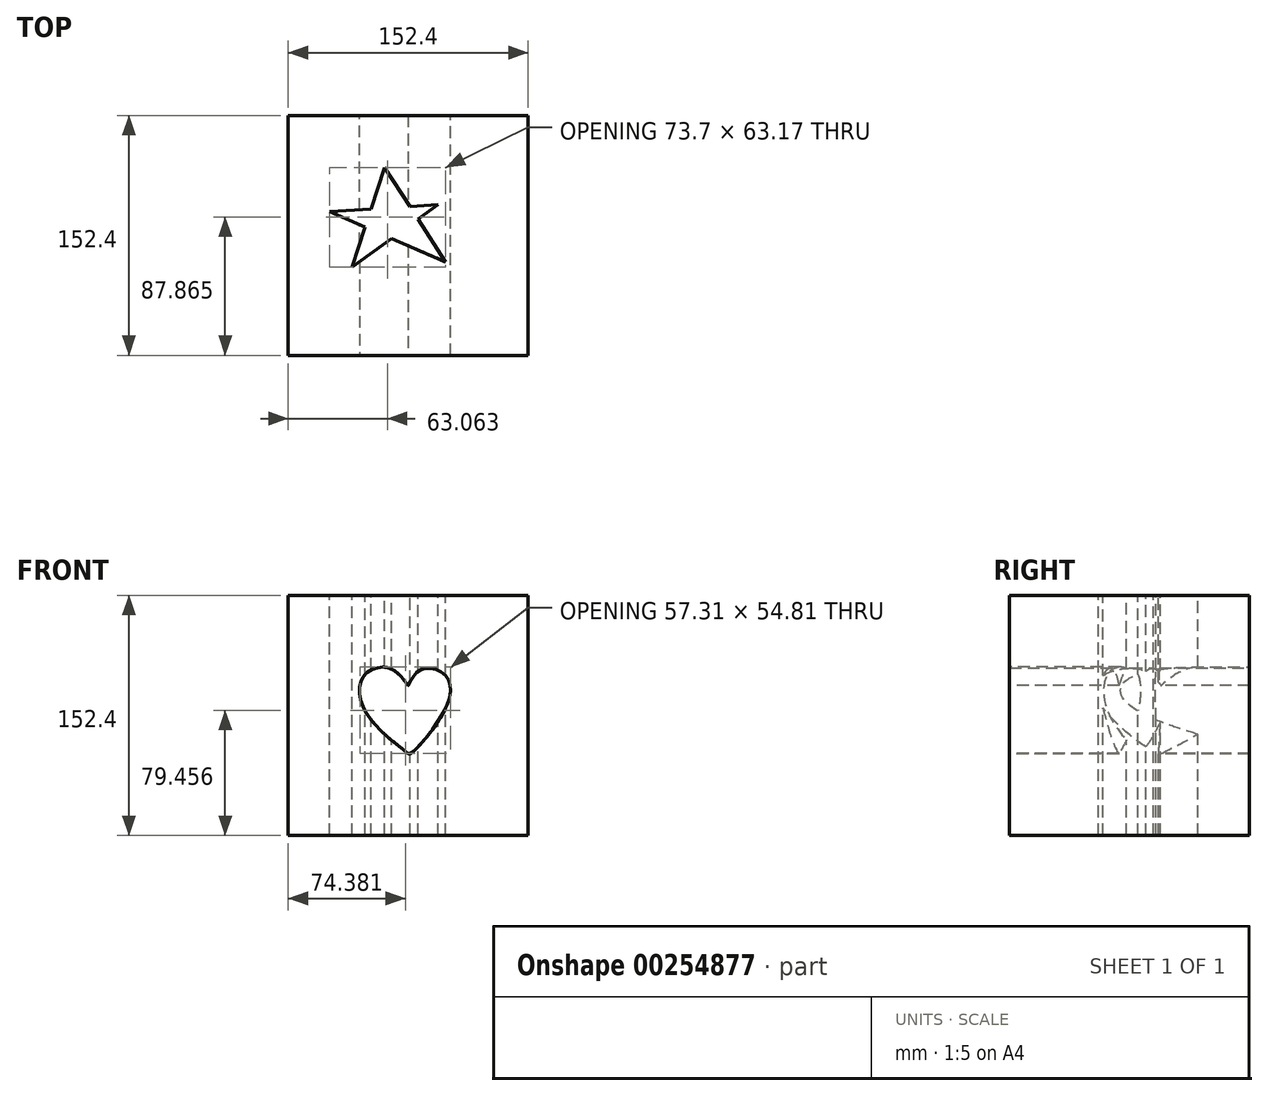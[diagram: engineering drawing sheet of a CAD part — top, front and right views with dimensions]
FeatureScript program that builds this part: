
annotation { "Feature Type Name" : "Feature", "Feature Type Description" : "" }
export const myFeature = defineFeature(function(context is Context, id is Id, definition is map)
    precondition{}
    {
        {
            var Q0;
            Q0=qCreatedBy(makeId("Front.planeOp"),FACE);
            var sketch = newSketch(context, id + "F0", { "sketchPlane" : qUnion([Q0])});
            skLineSegment(sketch, "E0.bottom", {"start": v(76.2, 76.2) * mm, "end": v(-76.2, 76.2) * mm});
            skLineSegment(sketch, "E0.top", {"start": v(76.2, -76.2) * mm, "end": v(-76.2, -76.2) * mm});
            skLineSegment(sketch, "E0.left", {"start": v(76.2, 76.2) * mm, "end": v(76.2, -76.2) * mm});
            skLineSegment(sketch, "E0.right", {"start": v(-76.2, 76.2) * mm, "end": v(-76.2, -76.2) * mm});
            skPoint(sketch, "E0.middle", {"position": v(0, 0) * mm});
            skSolve(sketch);
        }
        {
            var Q0;
            Q0=makeQuery(id+"F0.imprint","IMPRINT",FACE,{"disambiguationData":[TD([[makeQuery(id+"F0.imprint","IMPRINT",EDGE,{"derivedFrom":sQuery(id+"F0.wireOp",EDGE,"E0.bottom")}),1.0]])]});
            extrude(context, id + "F1", {"entities" : qUnion([Q0]), "depth" : 152.4 * mm});
        }
        {
            var Q0;
            Q0=makeQuery(id+"F1.opExtrude","CAP_FACE",FACE,{"disambiguationData":[OSD([sQuery(id+"F0.wireOp",EDGE,"E0.bottom"),sQuery(id+"F0.wireOp",EDGE,"E0.top"),sQuery(id+"F0.wireOp",EDGE,"E0.left"),sQuery(id+"F0.wireOp",EDGE,"E0.right")])],"isStart":false});
            var sketch = newSketch(context, id + "F2", { "sketchPlane" : qUnion([Q0])});
            skFitSpline(sketch, "E1", {"points": [v(0, 18.99) * mm, v(-12.54, 30.23) * mm, v(-28.02, 25.26) * mm, v(-28.02, 4.24) * mm, v(0, -24.15) * mm], "startDerivative": vector(-50.45, 68.23) * mm, "endDerivative": vector(103.8, -81.13) * mm});
            skFitSpline(sketch, "E2", {"points": [v(0, 18.99) * mm, v(8.85, 29.5) * mm, v(23.78, 25.26) * mm, v(23.6, 4.42) * mm, v(1.47, -24.15) * mm, v(0, -24.15) * mm], "startDerivative": vector(36, 71.1) * mm, "endDerivative": vector(-17.61, 8.59) * mm});
            skSolve(sketch);
        }
        {
            var Q0;
            Q0 = qSketchRegion(id + "F2", true);
            extrude(context, id + "F3", {"entities" : qUnion([Q0]), "operationType" : NewBodyOperationType.REMOVE, "endBound" : BoundingType.THROUGH_ALL, "oppositeDirection" : true, "depth" : 25.4 * mm});
        }
        {
            var Q0;
            Q0=makeQuery(id+"F1.opExtrude","SWEPT_FACE",FACE,{"disambiguationData":[OSD([sQuery(id+"F0.wireOp",EDGE,"E0.bottom")])]});
            var sketch = newSketch(context, id + "F4", { "sketchPlane" : qUnion([Q0])});
            skLineSegment(sketch, "E3", {"start": v(-35.51, -96.12) * mm, "end": v(-14.9, -32.95) * mm});
            skLineSegment(sketch, "E4", {"start": v(-14.9, -32.95) * mm, "end": v(23.71, -93.05) * mm});
            skLineSegment(sketch, "E5", {"start": v(23.71, -93.05) * mm, "end": v(-49.99, -61.03) * mm});
            skLineSegment(sketch, "E6", {"start": v(-49.99, -61.03) * mm, "end": v(18.89, -56.64) * mm});
            skLineSegment(sketch, "E7", {"start": v(18.89, -56.64) * mm, "end": v(-35.51, -96.12) * mm});
            skSolve(sketch);
        }
        {
            var Q0;
            Q0 = qSketchRegion(id + "F4", true);
            extrude(context, id + "F5", {"entities" : qUnion([Q0]), "operationType" : NewBodyOperationType.REMOVE, "endBound" : BoundingType.THROUGH_ALL, "oppositeDirection" : true, "depth" : 25.4 * mm});
        }
    });
